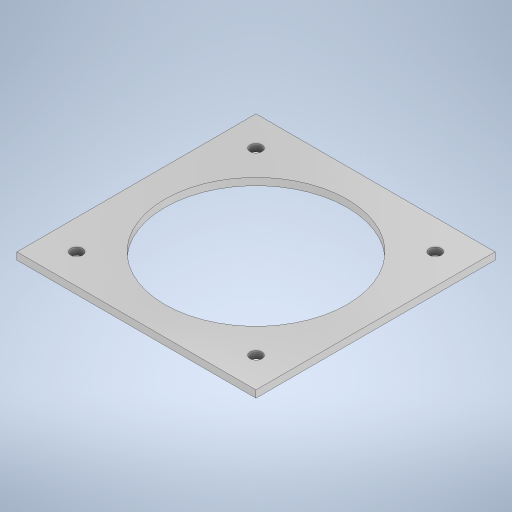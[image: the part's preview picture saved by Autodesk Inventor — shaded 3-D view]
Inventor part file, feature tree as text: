
AUTODESK INVENTOR PART (.ipt)
format: ipt  version: 2024 (Build 280153000, 153)  size: 250,880 bytes
history: native  units: in
note: dims shown in document units (in); Inventor stores cm internally (conversion verified against a paired STEP export)
features: sketch x3, hole x2, extrude x1
ambient origin geometry x8: Origin, YZ Plane, XZ Plane, XY Plane, X Axis, Y Axis, Z Axis, Center Point
bodies: Solid1 (feature_tree)
feature tree (6):
  extrude  "Extrusion1"  Depth=3.937in
  hole  "Hole1"  [1 undecoded]
  hole  "Hole2"  [1 undecoded]
  sketch  "Sketch1"  dims[d0=3.937in d1=3.937in]
  sketch  "Sketch2"  dims[d2=0.1181in d3=0.0in]
  sketch  "Sketch3"  dims[d4=3.0039in d5=0.2953in d6=0.1476in d7=0.0984in d8=90.0deg d9=0.3937in d10=0.8108in d11=0.1969in d12=0.2953in d13=0.1476in d14=0.0984in d15=90.0deg d16=0.3937in d17=0.8108in d18=0.4921in d19=0.4921in d20=1.5748in d22=360.0deg]
note: 2 required parameter values undecoded (feature->parameter linkage not recoverable at this tier; creation-order binding heuristic only, values carry confidence <= 0.55)
